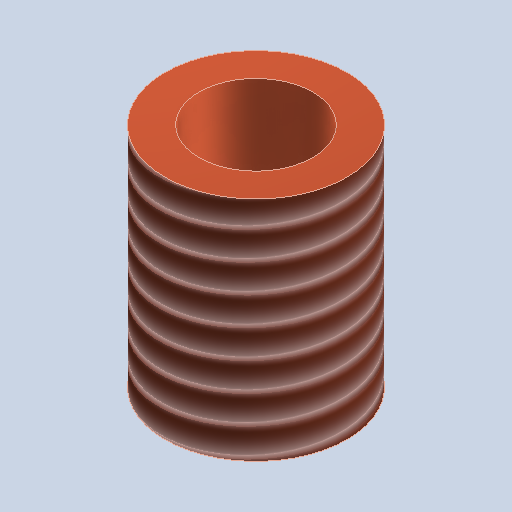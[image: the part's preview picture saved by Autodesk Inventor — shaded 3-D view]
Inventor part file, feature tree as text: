
AUTODESK INVENTOR PART (.ipt)
format: ipt  version: 2025.1 (Build 291241000, 241)  size: 293,888 bytes
history: native  units: mm
features: sketch x2, extrude x1, hole x1, thread x1
ambient origin geometry x8: Origin, YZ Plane, XZ Plane, XY Plane, X Axis, Y Axis, Z Axis, Center Point
bodies: Solid1 (feature_tree)
feature tree (5):
  extrude  "Extrusion1"  Depth=10.0mm TaperAngle=0.0deg
  hole  "Hole1"  [1 undecoded]
  thread  "Thread1"  [1 undecoded]
  sketch  "Sketch1"  dims[d0=8.0mm d1=10.0mm d2=0.0mm]
  sketch  "Sketch2"  dims[d3=5.0mm d4=6.0mm d5=4.0mm d6=2.0mm d7=90.0deg d8=8.0mm d9=0.0mm d10=11.0mm d11=0.0mm]
note: 2 required parameter values undecoded (feature->parameter linkage not recoverable at this tier; creation-order binding heuristic only, values carry confidence <= 0.55)
